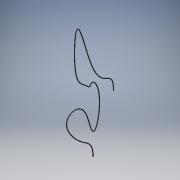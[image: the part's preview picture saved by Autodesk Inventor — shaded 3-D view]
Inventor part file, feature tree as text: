
AUTODESK INVENTOR PART (.ipt)
format: ipt  version: 2021 (Build 250183000, 183)  size: 254,464 bytes
history: native  units: in
note: dims shown in document units (in); Inventor stores cm internally (conversion verified against a paired STEP export)
features: sketch x3, plane x1, sweep x1
ambient origin geometry x8: Origin, YZ Plane, XZ Plane, XY Plane, X Axis, Y Axis, Z Axis, Center Point
bodies: Body1 (feature_tree)
feature tree (5):
  sketch  "Sketch1"  dims[d1=0.0in d2=0.0in]
  sketch  "Sketch2"
  plane  "Work Plane1"
  sweep  "Sweep2"
  sketch  "Sketch3"
